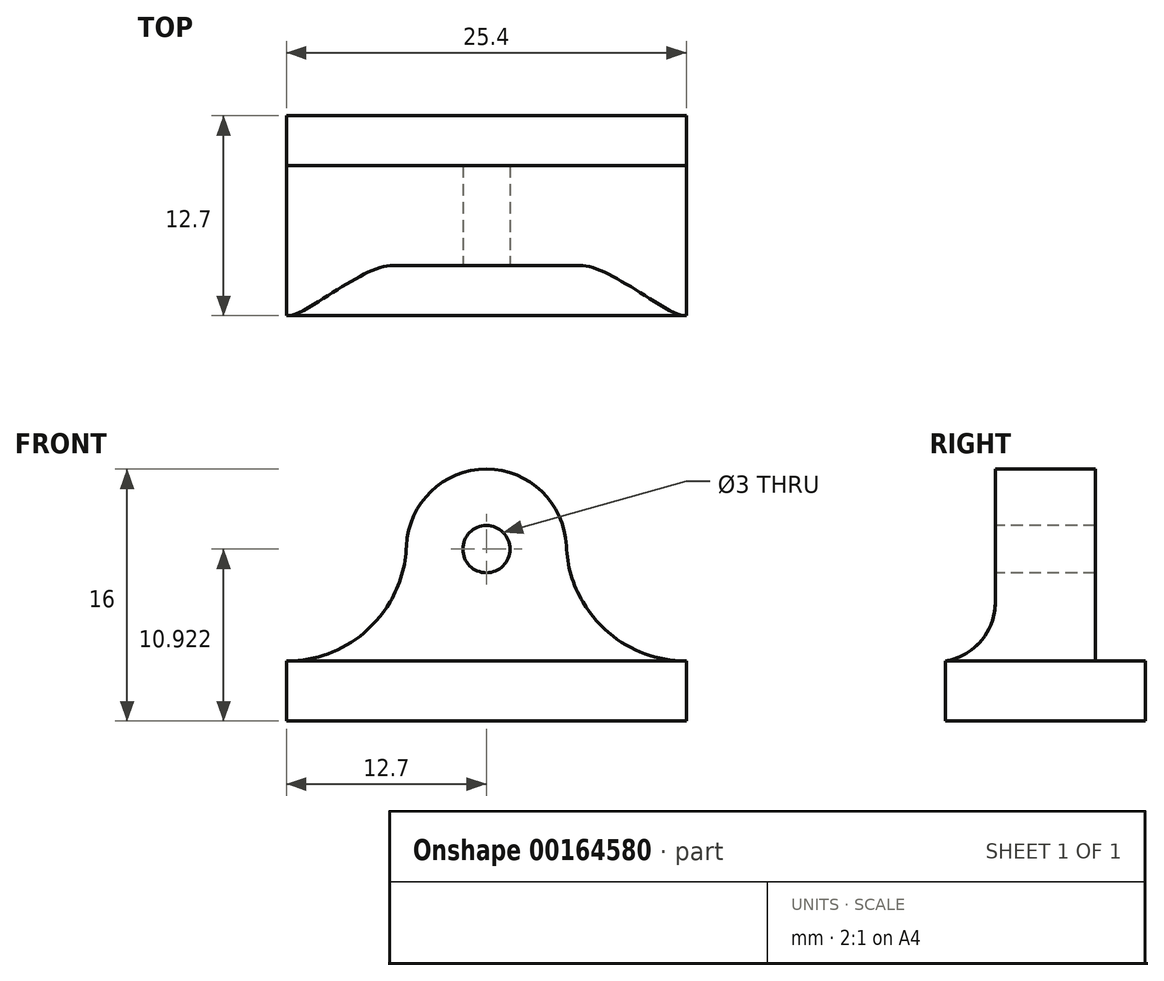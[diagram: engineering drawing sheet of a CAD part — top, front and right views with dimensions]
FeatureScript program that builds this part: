
annotation { "Feature Type Name" : "Feature", "Feature Type Description" : "" }
export const myFeature = defineFeature(function(context is Context, id is Id, definition is map)
    precondition{}
    {
        {
            var Q0;
            Q0=qCreatedBy(makeId("Top.planeOp"),FACE);
            var sketch = newSketch(context, id + "F0", { "sketchPlane" : qUnion([Q0])});
            skLineSegment(sketch, "E0.bottom", {"start": v(0, 0) * mm, "end": v(25.4, 0) * mm});
            skLineSegment(sketch, "E0.top", {"start": v(0, 12.7) * mm, "end": v(25.4, 12.7) * mm});
            skLineSegment(sketch, "E0.left", {"start": v(0, 0) * mm, "end": v(0, 12.7) * mm});
            skLineSegment(sketch, "E0.right", {"start": v(25.4, 0) * mm, "end": v(25.4, 12.7) * mm});
            skLineSegment(sketch, "E1.bottom", {"start": v(17.78, 3.18) * mm, "end": v(7.62, 3.17) * mm});
            skLineSegment(sketch, "E1.top", {"start": v(17.78, 9.53) * mm, "end": v(7.62, 9.53) * mm});
            skLineSegment(sketch, "E1.left", {"start": v(17.78, 3.18) * mm, "end": v(17.78, 9.53) * mm});
            skLineSegment(sketch, "E1.right", {"start": v(7.62, 3.17) * mm, "end": v(7.62, 9.53) * mm});
            skPoint(sketch, "E1.middle", {"position": v(12.7, 6.35) * mm});
            skPoint(sketch, "E1.middle.positionSnap0", {"position": v(0, 6.35) * mm});
            skPoint(sketch, "E1.middle.positionSnap1", {"position": v(12.7, 12.7) * mm});
            skPoint(sketch, "E1.centerSnap0", {"position": v(0, 6.35) * mm});
            skPoint(sketch, "E1.centerSnap1", {"position": v(12.7, 12.7) * mm});
            skSolve(sketch);
        }
        {
            var Q0;
            Q0=makeQuery(id+"F0.imprint","IMPRINT",FACE,{"disambiguationData":[TD([[makeQuery(id+"F0.imprint","IMPRINT",EDGE,{"derivedFrom":sQuery(id+"F0.wireOp",EDGE,"E0.bottom")}),1.0]])]});
            var Q1;
            Q1=makeQuery(id+"F0.imprint","IMPRINT",FACE,{"disambiguationData":[TD([[makeQuery(id+"F0.imprint","IMPRINT",EDGE,{"derivedFrom":sQuery(id+"F0.wireOp",EDGE,"E1.bottom")}),-1.0]])]});
            extrude(context, id + "F1", {"entities" : qUnion([Q0, Q1]), "depth" : 3.8 * mm});
        }
        {
            var Q0;
            Q0=makeQuery(id+"F0.imprint","IMPRINT",FACE,{"disambiguationData":[TD([[makeQuery(id+"F0.imprint","IMPRINT",EDGE,{"derivedFrom":sQuery(id+"F0.wireOp",EDGE,"E1.bottom")}),-1.0]])]});
            extrude(context, id + "F2", {"entities" : qUnion([Q0]), "operationType" : NewBodyOperationType.ADD, "depth" : 10.92 * mm});
        }
        {
            var Q0;
            Q0=makeQuery(id+"F2.opExtrude","SWEPT_FACE",FACE,{"disambiguationData":[OSD([sQuery(id+"F0.wireOp",EDGE,"E1.bottom")])]});
            var sketch = newSketch(context, id + "F3", { "sketchPlane" : qUnion([Q0])});
            skCircle(sketch, "E2", {"center": v(12.7, 10.92) * mm, "radius": 5.08 * mm});
            skSolve(sketch);
        }
        {
            var Q0;
            Q0 = qSketchRegion(id + "F3", true);
            var Q1;
            Q1=makeQuery(id+"F2.opExtrude","SWEPT_FACE",FACE,{"disambiguationData":[OSD([sQuery(id+"F0.wireOp",EDGE,"E1.top")])]});
            extrude(context, id + "F4", {"entities" : qUnion([Q0]), "operationType" : NewBodyOperationType.ADD, "endBound" : BoundingType.UP_TO_SURFACE, "oppositeDirection" : true, "endBoundEntityFace" : qUnion([Q1]), "depth" : 25.4 * mm});
        }
        {
            var Q0;
            Q0=makeQuery(id+"F4.boolean.opBoolean","MERGE",FACE,{"derivedFrom":[makeQuery(id+"F2.opExtrude","SWEPT_FACE",FACE,{"disambiguationData":[OSD([sQuery(id+"F0.wireOp",EDGE,"E1.bottom")])]}),makeQuery(id+"F4.opExtrude","CAP_FACE",FACE,{"disambiguationData":[OSD([sQuery(id+"F3.wireOp",EDGE,"E2")])],"isStart":true})]});
            var sketch = newSketch(context, id + "F5", { "sketchPlane" : qUnion([Q0])});
            skCircle(sketch, "E3", {"center": v(12.7, 10.92) * mm, "radius": 1.5 * mm});
            skSolve(sketch);
        }
        {
            var Q0;
            Q0 = qSketchRegion(id + "F5", true);
            extrude(context, id + "F6", {"entities" : qUnion([Q0]), "operationType" : NewBodyOperationType.REMOVE, "oppositeDirection" : true, "depth" : 25.4 * mm});
        }
        {
            var Q0;
            Q0=makeQuery(id+"F2.boolean.opBoolean","INTERSECT",EDGE,{"derivedFrom":[makeQuery(id+"F1.opExtrude","CAP_FACE",FACE,{"disambiguationData":[OSD([sQuery(id+"F0.wireOp",EDGE,"E0.bottom"),sQuery(id+"F0.wireOp",EDGE,"E0.top"),sQuery(id+"F0.wireOp",EDGE,"E0.left"),sQuery(id+"F0.wireOp",EDGE,"E0.right")])],"isStart":false}),makeQuery(id+"F2.opExtrude","SWEPT_FACE",FACE,{"disambiguationData":[OSD([sQuery(id+"F0.wireOp",EDGE,"E1.right")])]})]});
            var Q1;
            Q1=makeQuery(id+"F2.boolean.opBoolean","INTERSECT",EDGE,{"derivedFrom":[makeQuery(id+"F1.opExtrude","CAP_FACE",FACE,{"disambiguationData":[OSD([sQuery(id+"F0.wireOp",EDGE,"E0.bottom"),sQuery(id+"F0.wireOp",EDGE,"E0.top"),sQuery(id+"F0.wireOp",EDGE,"E0.left"),sQuery(id+"F0.wireOp",EDGE,"E0.right")])],"isStart":false}),makeQuery(id+"F2.opExtrude","SWEPT_FACE",FACE,{"disambiguationData":[OSD([sQuery(id+"F0.wireOp",EDGE,"E1.left")])]})]});
            fillet(context, id + "F7", {"entities" : qUnion([Q0, Q1]), "radius" : 7.62 * mm, "tangentPropagation" : true, "allowEdgeOverflow" : false});
        }
        {
            var Q0;
            Q0=makeQuery(id+"F2.boolean.opBoolean","INTERSECT",EDGE,{"derivedFrom":[makeQuery(id+"F1.opExtrude","CAP_FACE",FACE,{"disambiguationData":[OSD([sQuery(id+"F0.wireOp",EDGE,"E0.bottom"),sQuery(id+"F0.wireOp",EDGE,"E0.top"),sQuery(id+"F0.wireOp",EDGE,"E0.left"),sQuery(id+"F0.wireOp",EDGE,"E0.right")])],"isStart":false}),makeQuery(id+"F2.opExtrude","SWEPT_FACE",FACE,{"disambiguationData":[OSD([sQuery(id+"F0.wireOp",EDGE,"E1.bottom")])]})]});
            fillet(context, id + "F8", {"entities" : qUnion([Q0]), "radius" : 3.8 * mm, "tangentPropagation" : true, "allowEdgeOverflow" : false});
        }
    });
